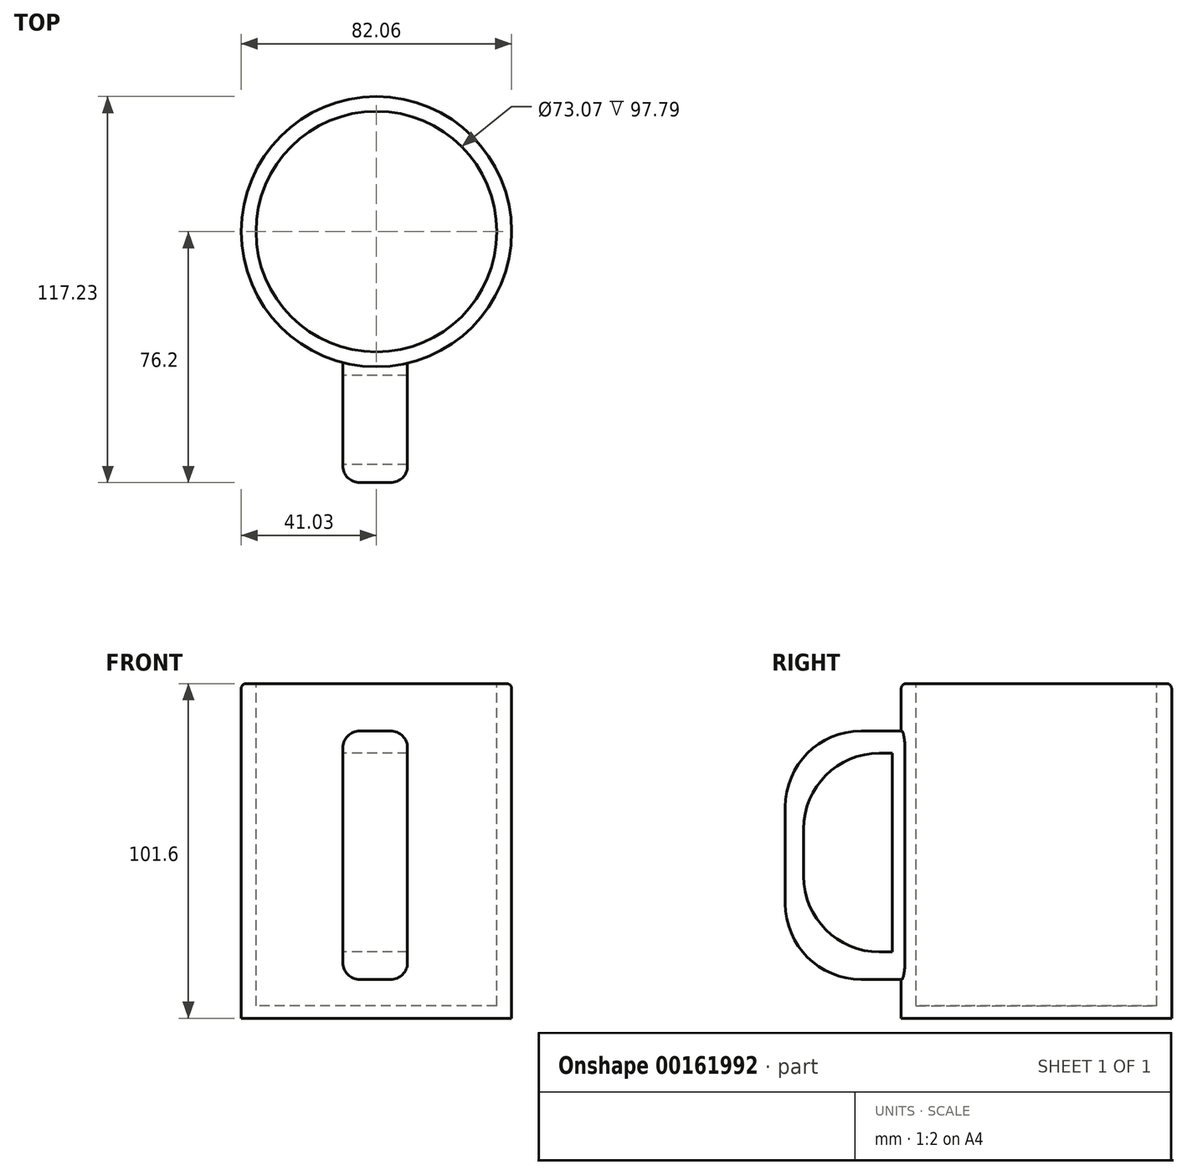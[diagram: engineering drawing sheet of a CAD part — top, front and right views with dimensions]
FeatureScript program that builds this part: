
annotation { "Feature Type Name" : "Feature", "Feature Type Description" : "" }
export const myFeature = defineFeature(function(context is Context, id is Id, definition is map)
    precondition{}
    {
        {
            var Q0;
            Q0=qCreatedBy(makeId("Top.planeOp"),FACE);
            var sketch = newSketch(context, id + "F0", { "sketchPlane" : qUnion([Q0])});
            skCircle(sketch, "E0", {"center": v(0, 0) * mm, "radius": 41.03 * mm});
            skSolve(sketch);
        }
        {
            var Q0;
            Q0=makeQuery(id+"F0.imprint","IMPRINT",FACE,{"disambiguationData":[TD([[makeQuery(id+"F0.imprint","IMPRINT",EDGE,{"derivedFrom":sQuery(id+"F0.wireOp",EDGE,"E0")}),1.0]])]});
            extrude(context, id + "F1", {"entities" : qUnion([Q0]), "depth" : 101.6 * mm});
        }
        {
            var Q0;
            Q0=makeQuery(id+"F1.opExtrude","CAP_FACE",FACE,{"disambiguationData":[OSD([sQuery(id+"F0.wireOp",EDGE,"E0")])],"isStart":false});
            var sketch = newSketch(context, id + "F2", { "sketchPlane" : qUnion([Q0])});
            skCircle(sketch, "E1", {"center": v(0, 0) * mm, "radius": 36.54 * mm});
            skSolve(sketch);
        }
        {
            var Q0;
            Q0=makeQuery(id+"F2.imprint","IMPRINT",FACE,{"disambiguationData":[TD([[makeQuery(id+"F2.imprint","IMPRINT",EDGE,{"derivedFrom":sQuery(id+"F2.wireOp",EDGE,"E1")}),1.0]])]});
            extrude(context, id + "F3", {"entities" : qUnion([Q0]), "operationType" : NewBodyOperationType.REMOVE, "oppositeDirection" : true, "depth" : 97.8 * mm});
        }
        {
            var Q0;
            Q0=makeQuery(id+"F3.boolean.opBoolean","COPY",EDGE,{"derivedFrom":makeQuery(id+"F3.opExtrude","CAP_EDGE",EDGE,{"disambiguationData":[OSD([sQuery(id+"F2.wireOp",EDGE,"E1")])],"isStart":true})});
            var Q1;
            Q1=makeQuery(id+"F1.opExtrude","CAP_EDGE",EDGE,{"disambiguationData":[OSD([sQuery(id+"F0.wireOp",EDGE,"E0")])],"isStart":false});
            fillet(context, id + "F4", {"entities" : qUnion([Q0, Q1]), "radius" : 1.53 * mm, "tangentPropagation" : true, "allowEdgeOverflow" : false});
        }
        {
            var Q0;
            Q0=qCreatedBy(makeId("Front.planeOp"),FACE);
            cPlane(context, id + "F5", {"entities" : qUnion([Q0]), "cplaneType" : CPlaneType.OFFSET, "offset" : 76.2 * mm, "width" : 152.4 * mm, "height" : 152.4 * mm});
        }
        {
            var Q0;
            Q0=qCreatedBy(id+"F5.planeOp",FACE);
            var sketch = newSketch(context, id + "F6", { "sketchPlane" : qUnion([Q0])});
            skLineSegment(sketch, "E2.bottom", {"start": v(-10.15, 87.2) * mm, "end": v(9.43, 87.2) * mm});
            skLineSegment(sketch, "E2.top", {"start": v(-10.15, 11.8) * mm, "end": v(9.43, 11.8) * mm});
            skLineSegment(sketch, "E2.left", {"start": v(-10.15, 87.2) * mm, "end": v(-10.15, 11.8) * mm});
            skLineSegment(sketch, "E2.right", {"start": v(9.43, 87.2) * mm, "end": v(9.43, 11.8) * mm});
            skSolve(sketch);
        }
        {
            var Q0;
            Q0=makeQuery(id+"F6.imprint","IMPRINT",FACE,{"disambiguationData":[TD([[makeQuery(id+"F6.imprint","IMPRINT",EDGE,{"derivedFrom":sQuery(id+"F6.wireOp",EDGE,"E2.bottom")}),-1.0]])]});
            var Q1;
            Q1=makeQuery(id+"F1.opExtrude","SWEPT_FACE",FACE,{"disambiguationData":[OSD([sQuery(id+"F0.wireOp",EDGE,"E0")])]});
            extrude(context, id + "F7", {"entities" : qUnion([Q0]), "operationType" : NewBodyOperationType.ADD, "endBound" : BoundingType.UP_TO_SURFACE, "oppositeDirection" : true, "endBoundEntityFace" : qUnion([Q1]), "depth" : 37.46 * mm});
        }
        {
            var Q0;
            Q0=makeQuery(id+"F7.opExtrude","SWEPT_FACE",FACE,{"disambiguationData":[OSD([sQuery(id+"F6.wireOp",EDGE,"E2.left")])]});
            var sketch = newSketch(context, id + "F8", { "sketchPlane" : qUnion([Q0])});
            skLineSegment(sketch, "E3.bottom", {"start": v(43.7, 80.48) * mm, "end": v(70.65, 80.48) * mm});
            skLineSegment(sketch, "E3.top", {"start": v(43.7, 20.12) * mm, "end": v(70.65, 20.12) * mm});
            skLineSegment(sketch, "E3.left", {"start": v(43.7, 80.48) * mm, "end": v(43.7, 20.12) * mm});
            skLineSegment(sketch, "E3.right", {"start": v(70.65, 80.48) * mm, "end": v(70.65, 20.12) * mm});
            skSolve(sketch);
        }
        {
            var Q0;
            Q0=makeQuery(id+"F8.imprint","IMPRINT",FACE,{"disambiguationData":[TD([[makeQuery(id+"F8.imprint","IMPRINT",EDGE,{"derivedFrom":sQuery(id+"F8.wireOp",EDGE,"E3.bottom")}),-1.0]])]});
            extrude(context, id + "F9", {"entities" : qUnion([Q0]), "operationType" : NewBodyOperationType.REMOVE, "endBound" : BoundingType.THROUGH_ALL, "oppositeDirection" : true, "depth" : 25.4 * mm});
        }
        {
            var Q0;
            Q0=makeQuery(id+"F7.opExtrude","CAP_EDGE",EDGE,{"disambiguationData":[OSD([sQuery(id+"F6.wireOp",EDGE,"E2.bottom")])],"isStart":true});
            var Q1;
            Q1=makeQuery(id+"F7.opExtrude","CAP_EDGE",EDGE,{"disambiguationData":[OSD([sQuery(id+"F6.wireOp",EDGE,"E2.top")])],"isStart":true});
            var Q2;
            Q2=makeQuery(id+"F9.boolean.opBoolean","COPY",EDGE,{"derivedFrom":makeQuery(id+"F9.opExtrude","SWEPT_EDGE",EDGE,{"disambiguationData":[OSD([sQuery(id+"F8.wireOp",EDGE,"E3.top"),sQuery(id+"F8.wireOp",EDGE,"E3.right")])]})});
            var Q3;
            Q3=makeQuery(id+"F9.boolean.opBoolean","COPY",EDGE,{"derivedFrom":makeQuery(id+"F9.opExtrude","SWEPT_EDGE",EDGE,{"disambiguationData":[OSD([sQuery(id+"F8.wireOp",EDGE,"E3.bottom"),sQuery(id+"F8.wireOp",EDGE,"E3.right")])]})});
            fillet(context, id + "F10", {"entities" : qUnion([Q0, Q1, Q2, Q3]), "radius" : 23 * mm, "tangentPropagation" : true, "allowEdgeOverflow" : false});
        }
        {
            var Q0;
            Q0=makeQuery(id+"F10.opFillet","BLEND_EDGE",EDGE,{"blendedFrom":[makeQuery(id+"F7.opExtrude","CAP_EDGE",EDGE,{"disambiguationData":[OSD([sQuery(id+"F6.wireOp",EDGE,"E2.bottom")])],"isStart":true}),makeQuery(id+"F7.opExtrude","SWEPT_FACE",FACE,{"disambiguationData":[OSD([sQuery(id+"F6.wireOp",EDGE,"E2.left")])]})],"blendedInto":[makeQuery(id+"F7.opExtrude","SWEPT_FACE",FACE,{"disambiguationData":[OSD([sQuery(id+"F6.wireOp",EDGE,"E2.left")])]})]});
            fillet(context, id + "F11", {"entities" : qUnion([Q0]), "radius" : 5.08 * mm, "tangentPropagation" : true, "allowEdgeOverflow" : false});
        }
        {
            var Q0;
            Q0=makeQuery(id+"F10.opFillet","BLEND_EDGE",EDGE,{"blendedFrom":[makeQuery(id+"F7.opExtrude","CAP_EDGE",EDGE,{"disambiguationData":[OSD([sQuery(id+"F6.wireOp",EDGE,"E2.bottom")])],"isStart":true}),makeQuery(id+"F7.opExtrude","SWEPT_FACE",FACE,{"disambiguationData":[OSD([sQuery(id+"F6.wireOp",EDGE,"E2.right")])]})],"blendedInto":[makeQuery(id+"F7.opExtrude","SWEPT_FACE",FACE,{"disambiguationData":[OSD([sQuery(id+"F6.wireOp",EDGE,"E2.right")])]})]});
            fillet(context, id + "F12", {"entities" : qUnion([Q0]), "radius" : 5.08 * mm, "tangentPropagation" : true, "allowEdgeOverflow" : false});
        }
    });
